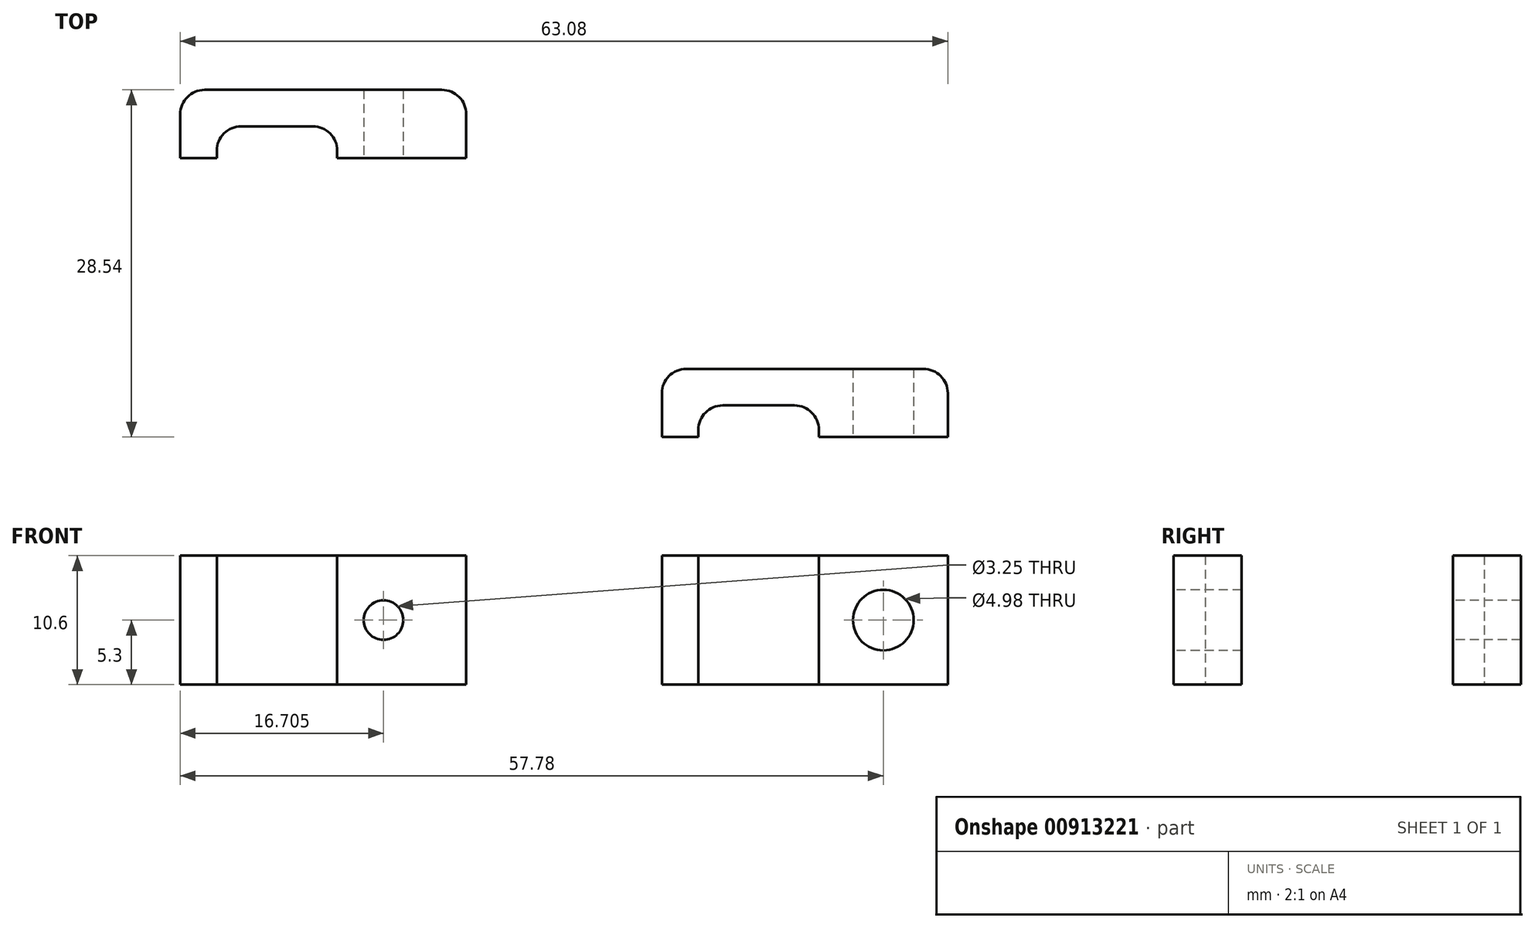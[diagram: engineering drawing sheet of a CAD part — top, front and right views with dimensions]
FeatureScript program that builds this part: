
annotation { "Feature Type Name" : "Feature", "Feature Type Description" : "" }
export const myFeature = defineFeature(function(context is Context, id is Id, definition is map)
    precondition{}
    {
        {
            var Q0;
            Q0=qCreatedBy(makeId("Top.planeOp"),FACE);
            var sketch = newSketch(context, id + "F0", { "sketchPlane" : qUnion([Q0])});
            skLineSegment(sketch, "E0", {"start": v(0, 0) * mm, "end": v(0, 2.6) * mm});
            skLineSegment(sketch, "E1", {"start": v(0, 2.6) * mm, "end": v(-9.9, 2.6) * mm});
            skLineSegment(sketch, "E2", {"start": v(-9.9, 2.6) * mm, "end": v(-9.9, 0) * mm});
            skLineSegment(sketch, "E3", {"start": v(-9.9, 0) * mm, "end": v(-12.9, 0) * mm});
            skLineSegment(sketch, "E4", {"start": v(-12.9, 0) * mm, "end": v(-12.9, 5.6) * mm});
            skLineSegment(sketch, "E5", {"start": v(-12.9, 5.6) * mm, "end": v(10.6, 5.6) * mm});
            skLineSegment(sketch, "E6", {"start": v(10.6, 5.6) * mm, "end": v(10.6, 0) * mm});
            skLineSegment(sketch, "E7", {"start": v(10.6, 0) * mm, "end": v(0, 0) * mm});
            skSolve(sketch);
        }
        {
            var Q0;
            Q0 = qSketchRegion(id + "F0", true);
            extrude(context, id + "F1", {"entities" : qUnion([Q0]), "depth" : 10.6 * mm, "offsetDistance" : 25 * mm});
        }
        {
            var Q0;
            Q0=makeQuery(id+"F1.opExtrude","SWEPT_FACE",FACE,{"disambiguationData":[OSD([sQuery(id+"F0.wireOp",EDGE,"E7")])]});
            var sketch = newSketch(context, id + "F2", { "sketchPlane" : qUnion([Q0])});
            skLineSegment(sketch, "E8", {"start": v(10.6, 10.6) * mm, "end": v(0, 0) * mm, "construction": true});
            skLineSegment(sketch, "E9", {"start": v(10.6, 0) * mm, "end": v(0, 10.6) * mm, "construction": true});
            skPoint(sketch, "E10", {"position": v(5.3, 5.3) * mm});
            skSolve(sketch);
        }
        {
            var Q0;
            Q0=sQuery(id+"F2.wireOp",VERTEX,"E10");
            var Q1;
            Q1=makeQuery(id+"F1.opExtrude","SWEPT_BODY",BODY,{"disambiguationData":[OSD([sQuery(id+"F0.wireOp",EDGE,"E0"),sQuery(id+"F0.wireOp",EDGE,"E1"),sQuery(id+"F0.wireOp",EDGE,"E2"),sQuery(id+"F0.wireOp",EDGE,"E3"),sQuery(id+"F0.wireOp",EDGE,"E4"),sQuery(id+"F0.wireOp",EDGE,"E5"),sQuery(id+"F0.wireOp",EDGE,"pGLl8j3l-TfzB-Mg1T-iY5R-NKUFIsoOqskJ"),sQuery(id+"F0.wireOp",EDGE,"ZBrT3yhz-rDVV-u8xU-sUrT-kTUKELfu4WxN"),sQuery(id+"F0.wireOp",EDGE,"E6"),sQuery(id+"F0.wireOp",EDGE,"E7")])]});
            hole(context, id + "F3", {"style" : HoleStyle.SIMPLE, "endStyle" : HoleEndStyle.THROUGH, "standardTappedOrClearance" : lookupTablePath({ "fit" : "Normal (ASME)", "standard" : "ANSI", "size" : "#8", "type" : "Clearance" }), "standardBlindInLast" : lookupTablePath({ "fit" : "Normal", "standard" : "ANSI", "size" : "#8", "type" : "Clearance" }), "holeDiameter" : 4.98 * mm, "majorDiameter" : 5 * mm, "isTappedThrough" : true, "tappedDepth" : 12 * mm, "tapClearance" : 3, "startFromSketch" : true, "locations" : qUnion([Q0]), "scope" : qUnion([Q1])});
        }
        {
            var Q0;
            Q0=makeQuery(id+"F1.opExtrude","SWEPT_EDGE",EDGE,{"disambiguationData":[OSD([sQuery(id+"F0.wireOp",EDGE,"E1"),sQuery(id+"F0.wireOp",EDGE,"E2")])]});
            var Q1;
            Q1=makeQuery(id+"F1.opExtrude","SWEPT_EDGE",EDGE,{"disambiguationData":[OSD([sQuery(id+"F0.wireOp",EDGE,"E0"),sQuery(id+"F0.wireOp",EDGE,"E1")])]});
            var Q2;
            Q2=makeQuery(id+"F1.opExtrude","SWEPT_EDGE",EDGE,{"disambiguationData":[OSD([sQuery(id+"F0.wireOp",EDGE,"E4"),sQuery(id+"F0.wireOp",EDGE,"E5")])]});
            var Q3;
            Q3=makeQuery(id+"F1.opExtrude","SWEPT_EDGE",EDGE,{"disambiguationData":[OSD([sQuery(id+"F0.wireOp",EDGE,"E5"),sQuery(id+"F0.wireOp",EDGE,"E6")])]});
            fillet(context, id + "F4", {"entities" : qUnion([Q0, Q1, Q2, Q3]), "radius" : 2 * mm, "tangentPropagation" : true, "allowEdgeOverflow" : false});
        }
        {
            var Q0;
            Q0=qCreatedBy(makeId("Top.planeOp"),FACE);
            var sketch = newSketch(context, id + "F5", { "sketchPlane" : qUnion([Q0])});
            skLineSegment(sketch, "E11", {"start": v(-39.58, 22.94) * mm, "end": v(-39.58, 25.54) * mm});
            skLineSegment(sketch, "E12", {"start": v(-39.58, 25.54) * mm, "end": v(-49.48, 25.54) * mm});
            skLineSegment(sketch, "E13", {"start": v(-49.48, 25.54) * mm, "end": v(-49.48, 22.94) * mm});
            skLineSegment(sketch, "E14", {"start": v(-49.48, 22.94) * mm, "end": v(-52.48, 22.94) * mm});
            skLineSegment(sketch, "E15", {"start": v(-52.48, 22.94) * mm, "end": v(-52.48, 28.54) * mm});
            skLineSegment(sketch, "E16", {"start": v(-52.48, 28.54) * mm, "end": v(-28.98, 28.54) * mm});
            skLineSegment(sketch, "E17", {"start": v(-28.98, 28.54) * mm, "end": v(-28.98, 22.94) * mm});
            skLineSegment(sketch, "E18", {"start": v(-28.98, 22.94) * mm, "end": v(-39.58, 22.94) * mm});
            skSolve(sketch);
        }
        {
            var Q0;
            Q0 = qSketchRegion(id + "F5", true);
            extrude(context, id + "F6", {"entities" : qUnion([Q0]), "depth" : 10.6 * mm, "offsetDistance" : 25 * mm});
        }
        {
            var Q0;
            Q0=makeQuery(id+"F6.opExtrude","SWEPT_FACE",FACE,{"disambiguationData":[OSD([sQuery(id+"F5.wireOp",EDGE,"E18")])]});
            var sketch = newSketch(context, id + "F7", { "sketchPlane" : qUnion([Q0])});
            skLineSegment(sketch, "E19", {"start": v(-28.97, 108.53) * mm, "end": v(-39.57, 97.93) * mm, "construction": true});
            skLineSegment(sketch, "E20", {"start": v(-28.97, 97.93) * mm, "end": v(-39.57, 108.53) * mm, "construction": true});
            skPoint(sketch, "E21", {"position": v(-34.27, 103.23) * mm});
            skLineSegment(sketch, "E22", {"start": v(-30.48, 10.6) * mm, "end": v(-41.08, 0) * mm, "construction": true});
            skLineSegment(sketch, "E23", {"start": v(-30.48, 0) * mm, "end": v(-41.08, 10.6) * mm, "construction": true});
            skPoint(sketch, "E24", {"position": v(-35.78, 5.3) * mm});
            skSolve(sketch);
        }
        {
            var Q0;
            Q0=sQuery(id+"F7.wireOp",VERTEX,"E24");
            var Q1;
            Q1=makeQuery(id+"F6.opExtrude","SWEPT_BODY",BODY,{"disambiguationData":[OSD([sQuery(id+"F5.wireOp",EDGE,"E11"),sQuery(id+"F5.wireOp",EDGE,"E12"),sQuery(id+"F5.wireOp",EDGE,"E13"),sQuery(id+"F5.wireOp",EDGE,"E14"),sQuery(id+"F5.wireOp",EDGE,"E15"),sQuery(id+"F5.wireOp",EDGE,"E16"),sQuery(id+"F5.wireOp",EDGE,"E17"),sQuery(id+"F5.wireOp",EDGE,"E18")])]});
            hole(context, id + "F8", {"style" : HoleStyle.SIMPLE, "endStyle" : HoleEndStyle.THROUGH, "standardTappedOrClearance" : lookupTablePath({ "fit" : "Normal (ASME)", "standard" : "ANSI", "size" : "#4", "type" : "Clearance" }), "standardBlindInLast" : lookupTablePath({ "fit" : "Normal", "standard" : "ANSI", "size" : "#4", "type" : "Clearance" }), "holeDiameter" : 3.25 * mm, "majorDiameter" : 5 * mm, "isTappedThrough" : true, "tappedDepth" : 12 * mm, "tapClearance" : 3, "startFromSketch" : true, "locations" : qUnion([Q0]), "scope" : qUnion([Q1])});
        }
        {
            var Q0;
            Q0=makeQuery(id+"F6.opExtrude","SWEPT_EDGE",EDGE,{"disambiguationData":[OSD([sQuery(id+"F5.wireOp",EDGE,"E12"),sQuery(id+"F5.wireOp",EDGE,"E13")])]});
            var Q1;
            Q1=makeQuery(id+"F6.opExtrude","SWEPT_EDGE",EDGE,{"disambiguationData":[OSD([sQuery(id+"F5.wireOp",EDGE,"E11"),sQuery(id+"F5.wireOp",EDGE,"E12")])]});
            var Q2;
            Q2=makeQuery(id+"F6.opExtrude","SWEPT_EDGE",EDGE,{"disambiguationData":[OSD([sQuery(id+"F5.wireOp",EDGE,"E15"),sQuery(id+"F5.wireOp",EDGE,"E16")])]});
            var Q3;
            Q3=makeQuery(id+"F6.opExtrude","SWEPT_EDGE",EDGE,{"disambiguationData":[OSD([sQuery(id+"F5.wireOp",EDGE,"E16"),sQuery(id+"F5.wireOp",EDGE,"E17")])]});
            fillet(context, id + "F9", {"entities" : qUnion([Q0, Q1, Q2, Q3]), "radius" : 2 * mm, "tangentPropagation" : true, "allowEdgeOverflow" : false});
        }
    });
